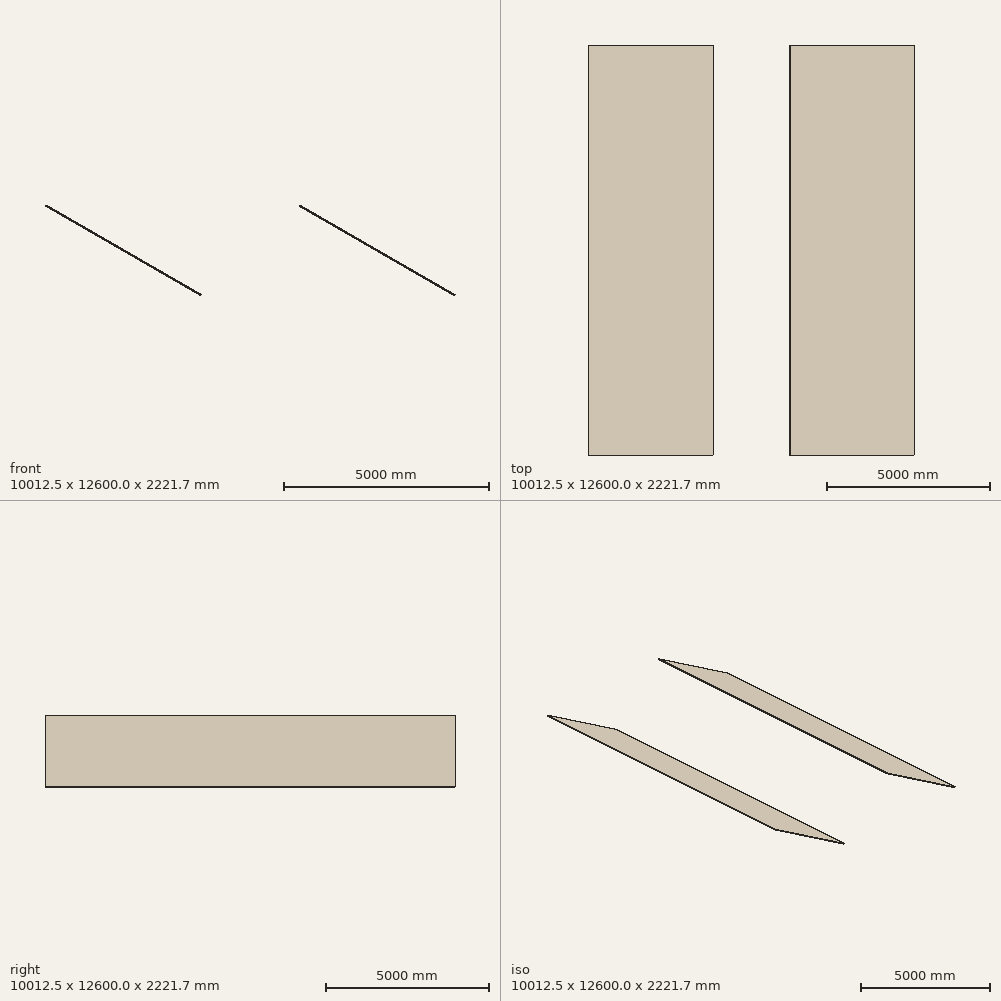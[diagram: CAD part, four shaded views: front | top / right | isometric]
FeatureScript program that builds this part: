
annotation { "Feature Type Name" : "Feature", "Feature Type Description" : "" }
export const myFeature = defineFeature(function(context is Context, id is Id, definition is map)
    precondition{}
    {
        {
            var Q0;
            Q0=qCreatedBy(makeId("Front.planeOp"),FACE);
            cPlane(context, id + "F0", {"entities" : qUnion([Q0]), "cplaneType" : CPlaneType.OFFSET, "offset" : 8000 * mm, "width" : 150 * mm, "height" : 150 * mm});
        }
        {
            var Q0;
            Q0=qCreatedBy(id+"F0.planeOp",FACE);
            var sketch = newSketch(context, id + "F1", { "sketchPlane" : qUnion([Q0])});
            skLineSegment(sketch, "E0", {"start": v(2000, 2200) * mm, "end": v(5810.51, 0) * mm});
            skLineSegment(sketch, "E1", {"start": v(5810.51, 0) * mm, "end": v(5823.01, 21.65) * mm});
            skLineSegment(sketch, "E2", {"start": v(5823.01, 21.65) * mm, "end": v(2012.5, 2221.65) * mm});
            skLineSegment(sketch, "E3", {"start": v(2012.5, 2221.65) * mm, "end": v(2000, 2200) * mm});
            skLineSegment(sketch, "E4", {"start": v(8189.49, 2200) * mm, "end": v(12000, 0) * mm});
            skLineSegment(sketch, "E5", {"start": v(12000, 0) * mm, "end": v(12012.5, 21.65) * mm});
            skLineSegment(sketch, "E6", {"start": v(12012.5, 21.65) * mm, "end": v(8201.99, 2221.65) * mm});
            skLineSegment(sketch, "E7", {"start": v(8201.99, 2221.65) * mm, "end": v(8189.49, 2200) * mm});
            skSolve(sketch);
        }
        {
            var Q0;
            Q0 = qSketchRegion(id + "F1", true);
            extrude(context, id + "F2", {"entities" : qUnion([Q0]), "depth" : 12600 * mm, "offsetDistance" : 25 * mm});
        }
    });
